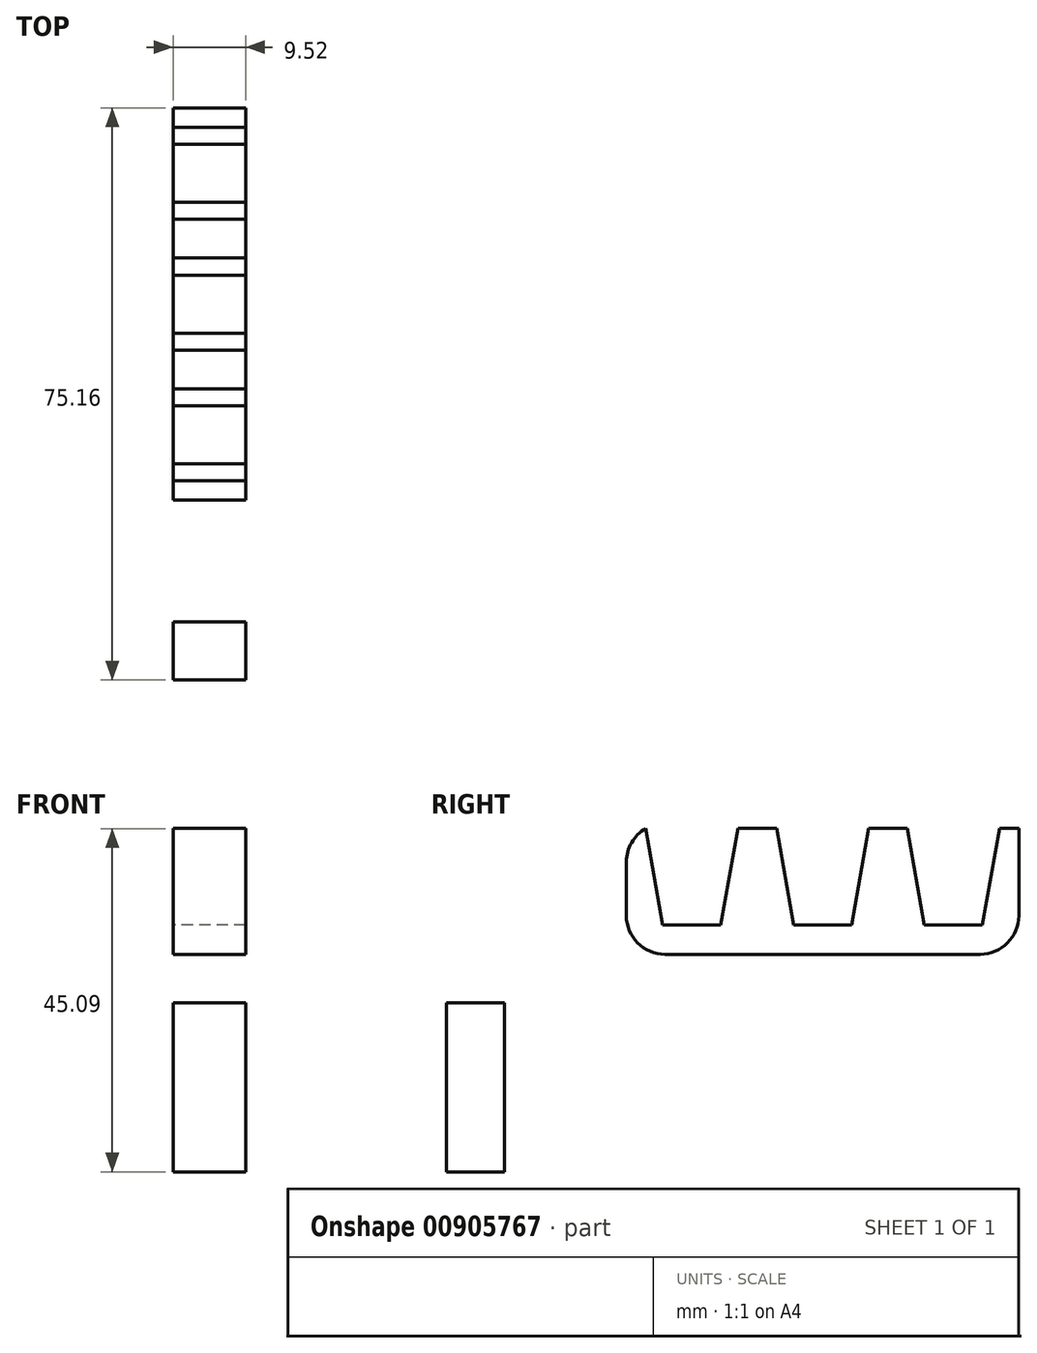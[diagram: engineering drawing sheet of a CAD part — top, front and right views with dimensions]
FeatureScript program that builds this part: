
annotation { "Feature Type Name" : "Feature", "Feature Type Description" : "" }
export const myFeature = defineFeature(function(context is Context, id is Id, definition is map)
    precondition{}
    {
        {
            var Q0;
            Q0=qCreatedBy(makeId("Right.planeOp"),FACE);
            var sketch = newSketch(context, id + "F0", { "sketchPlane" : qUnion([Q0])});
            skArc(sketch, "E0", {"start": v(-21.93, 3.94) * mm, "mid": v(-17.74, 8.13) * mm, "end": v(-13.55, 3.94) * mm});
            skLineSegment(sketch, "E1", {"start": v(-13.55, 3.94) * mm, "end": v(-13.55, -2.41) * mm});
            skLineSegment(sketch, "E2", {"start": v(-29.55, -8.76) * mm, "end": v(-29.55, -30.99) * mm});
            skLineSegment(sketch, "E3", {"start": v(-21.93, 3.94) * mm, "end": v(-21.93, 0.76) * mm});
            skLineSegment(sketch, "E4.0", {"start": v(-29.55, 3.94) * mm, "end": v(-29.55, 0.76) * mm});
            skArc(sketch, "E4.1", {"start": v(-29.55, 3.94) * mm, "mid": v(-18.38, 15.73) * mm, "end": v(-6, 5.21) * mm});
            skLineSegment(sketch, "E4.2", {"start": v(-5.93, 14.1) * mm, "end": v(-5.93, -2.41) * mm});
            skLineSegment(sketch, "E5.1", {"start": v(-21.93, -8.76) * mm, "end": v(-21.93, -30.99) * mm});
            skLineSegment(sketch, "E6", {"start": v(-29.55, -30.99) * mm, "end": v(-21.93, -30.99) * mm});
            skLineSegment(sketch, "E7", {"start": v(-29.55, 0.76) * mm, "end": v(-21.93, 0.76) * mm});
            skArc(sketch, "E8", {"start": v(-13.55, -2.41) * mm, "mid": v(-16.16, -7.67) * mm, "end": v(-21.93, -8.76) * mm});
            skLineSegment(sketch, "E9", {"start": v(-29.55, -8.76) * mm, "end": v(-21.93, -8.76) * mm});
            skArc(sketch, "E10.0", {"start": v(-5.93, -2.41) * mm, "mid": v(-10.75, -13.08) * mm, "end": v(-21.93, -16.52) * mm});
            skLineSegment(sketch, "E11", {"start": v(-5.93, 3.94) * mm, "end": v(-5.93, -2.41) * mm});
            skLineSegment(sketch, "E12.top", {"start": v(-5.93, -2.41) * mm, "end": v(45.6, -2.41) * mm});
            skLineSegment(sketch, "E12.right", {"start": v(45.6, 14.1) * mm, "end": v(45.6, -2.41) * mm});
            skLineSegment(sketch, "E13", {"start": v(-5.93, 14.1) * mm, "end": v(-3.39, 14.1) * mm});
            skLineSegment(sketch, "E14", {"start": v(-3.39, 14.1) * mm, "end": v(-1.15, 1.4) * mm});
            skLineSegment(sketch, "E15", {"start": v(-1.15, 1.4) * mm, "end": v(6.47, 1.4) * mm});
            skLineSegment(sketch, "E16", {"start": v(6.47, 1.4) * mm, "end": v(8.71, 14.1) * mm});
            skLineSegment(sketch, "E17", {"start": v(8.71, 14.1) * mm, "end": v(13.8, 14.1) * mm});
            skLineSegment(sketch, "E18", {"start": v(13.8, 14.1) * mm, "end": v(16.03, 1.4) * mm});
            skLineSegment(sketch, "E19", {"start": v(16.03, 1.4) * mm, "end": v(23.65, 1.4) * mm});
            skLineSegment(sketch, "E20", {"start": v(23.65, 1.4) * mm, "end": v(25.89, 14.1) * mm});
            skLineSegment(sketch, "E21", {"start": v(25.89, 14.1) * mm, "end": v(30.97, 14.1) * mm});
            skLineSegment(sketch, "E22", {"start": v(30.97, 14.1) * mm, "end": v(33.2, 1.4) * mm});
            skLineSegment(sketch, "E23", {"start": v(33.2, 1.4) * mm, "end": v(40.83, 1.4) * mm});
            skLineSegment(sketch, "E24", {"start": v(40.83, 1.4) * mm, "end": v(43.07, 14.1) * mm});
            skLineSegment(sketch, "E25", {"start": v(43.07, 14.1) * mm, "end": v(45.6, 14.1) * mm});
            skLineSegment(sketch, "E26", {"start": v(49.2, 1.4) * mm, "end": v(-10.18, 1.4) * mm, "construction": true});
            skPoint(sketch, "E27", {"position": v(-13.55, 1.4) * mm});
            skLineSegment(sketch, "E28", {"start": v(-5.93, 14.1) * mm, "end": v(-11.73, 14.1) * mm});
            skSolve(sketch);
        }
        {
            var Q0;
            Q0=makeQuery(id+"F0.imprint","IMPRINT",FACE,{"disambiguationData":[TD([[makeQuery(id+"F0.imprint","IMPRINT",EDGE,{"derivedFrom":sQuery(id+"F0.wireOp",EDGE,"E0")}),1.0]])]});
            var Q1;
            Q1=makeQuery(id+"F0.imprint","IMPRINT",FACE,{"disambiguationData":[TD([[makeQuery(id+"F0.imprint","IMPRINT",EDGE,{"derivedFrom":sQuery(id+"F0.wireOp",EDGE,"E2")}),1.0]])]});
            var Q2;
            {var subQ3=sQuery(id+"F0.wireOp",EDGE,"E4.2");Q2=makeQuery(id+"F0.imprint","IMPRINT",FACE,{"disambiguationData":[TD([[makeQuery(id+"F0.imprint","IMPRINT",EDGE,{"derivedFrom":subQ3}),1.0]])]});}
            var Q3;
            Q3=makeQuery(id+"F0.imprint","IMPRINT",FACE,{"disambiguationData":[TD([[makeQuery(id+"F0.imprint","IMPRINT",EDGE,{"derivedFrom":sQuery(id+"F0.wireOp",EDGE,"IVhdlBJh-vM5k-T7ff-ZNz9-fgUW7ZMvtMVS.top")}),1.0]])]});
            var Q4;
            Q4=makeQuery(id+"F0.imprint","IMPRINT",FACE,{"disambiguationData":[TD([[makeQuery(id+"F0.imprint","IMPRINT",EDGE,{"derivedFrom":sQuery(id+"F0.wireOp",EDGE,"IVhdlBJh-vM5k-T7ff-ZNz9-fgUW7ZMvtMVS.top")}),-1.0]])]});
            extrude(context, id + "F1", {"entities" : qUnion([Q0, Q1, Q2, Q3, Q4]), "depth" : 9.52 * mm, "offsetDistance" : 25.4 * mm, "symmetric" : true});
        }
        {
            var Q0;
            Q0=makeQuery(id+"F1.opExtrude","SWEPT_EDGE",EDGE,{"disambiguationData":[OSD([sQuery(id+"F0.wireOp",EDGE,"E12.top"),sQuery(id+"F0.wireOp",EDGE,"E12.right")])]});
            var Q1;
            Q1=makeQuery(id+"F1.opExtrude","SWEPT_EDGE",EDGE,{"disambiguationData":[OSD([sQuery(id+"F0.wireOp",EDGE,"E12.bottom"),sQuery(id+"F0.wireOp",EDGE,"IVhdlBJh-vM5k-T7ff-ZNz9-fgUW7ZMvtMVS.right")])]});
            var Q2;
            Q2=makeQuery(id+"F1.opExtrude","SWEPT_EDGE",EDGE,{"disambiguationData":[OSD([sQuery(id+"F0.wireOp",EDGE,"E4.1"),sQuery(id+"F0.wireOp",EDGE,"E4.2"),sQuery(id+"F0.wireOp",EDGE,"E12.bottom")])]});
            var Q3;
            Q3=makeQuery(id+"F1.opExtrude","SWEPT_EDGE",EDGE,{"disambiguationData":[OSD([sQuery(id+"F0.wireOp",EDGE,"E4.2"),sQuery(id+"F0.wireOp",EDGE,"E10.0"),sQuery(id+"F0.wireOp",EDGE,"E12.top")])]});
            fillet(context, id + "F2", {"entities" : qUnion([Q0, Q1, Q2, Q3]), "radius" : 5.08 * mm, "tangentPropagation" : true, "allowEdgeOverflow" : false});
        }
    });
